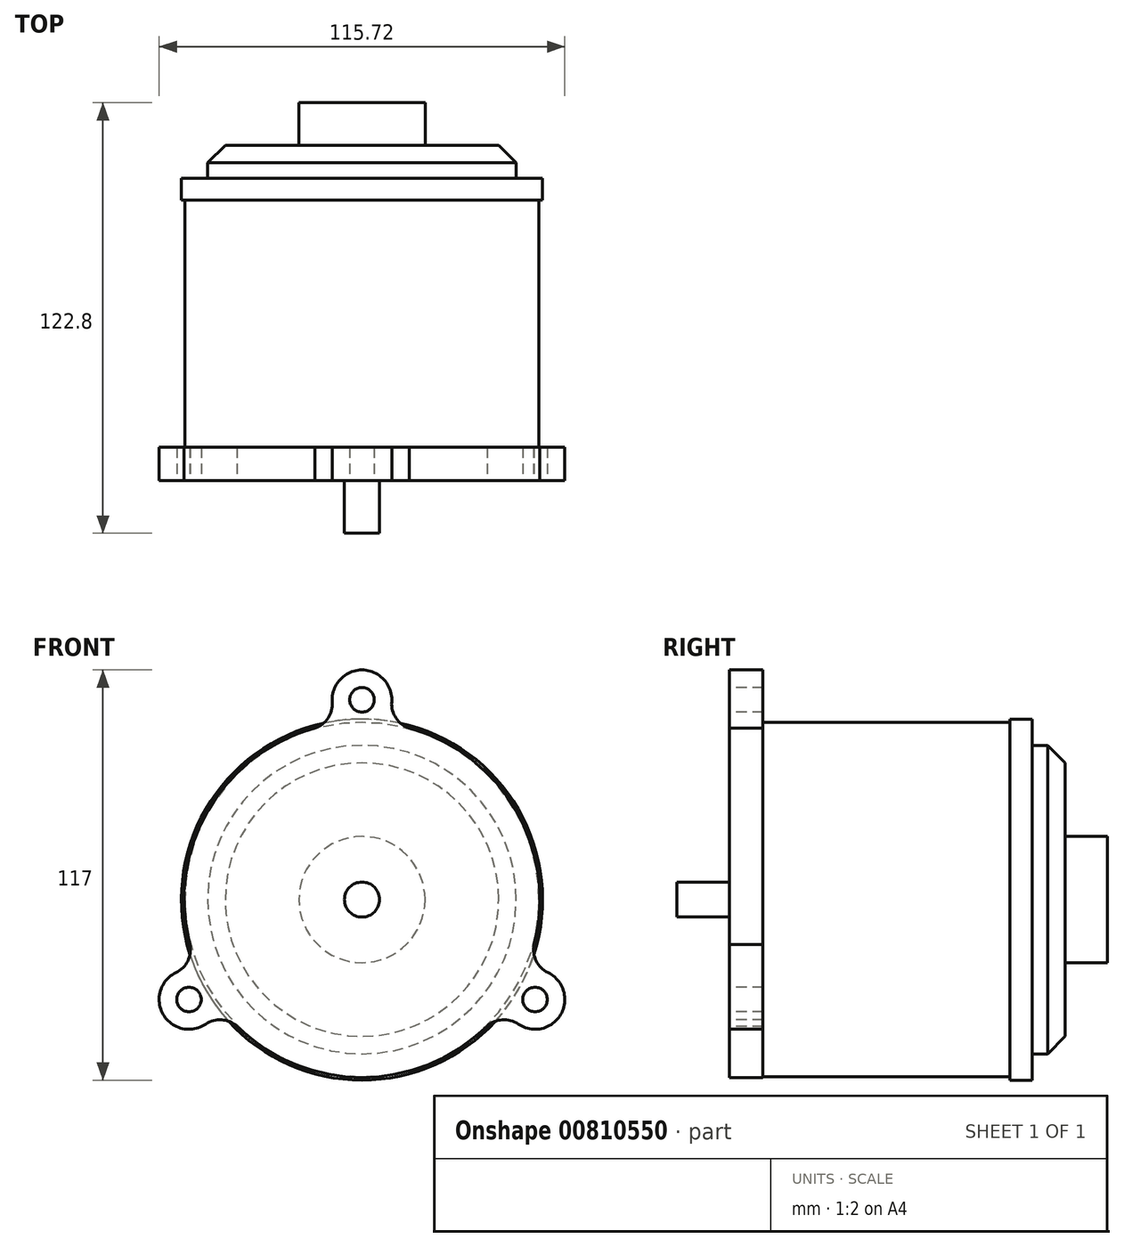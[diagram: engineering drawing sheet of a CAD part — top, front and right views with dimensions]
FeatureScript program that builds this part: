
annotation { "Feature Type Name" : "Feature", "Feature Type Description" : "" }
export const myFeature = defineFeature(function(context is Context, id is Id, definition is map)
    precondition{}
    {
        {
            var Q0;
            Q0=qCreatedBy(makeId("Front.planeOp"),FACE);
            var sketch = newSketch(context, id + "F0", { "sketchPlane" : qUnion([Q0])});
            skCircle(sketch, "E0", {"center": v(0, 0) * mm, "radius": 57 * mm, "construction": true});
            skArc(sketch, "E1", {"start": v(-13.46, 48.93) * mm, "mid": v(-43.95, 25.37) * mm, "end": v(-49.1, -12.81) * mm});
            skLineSegment(sketch, "E2", {"start": v(0, 0) * mm, "end": v(0, 70.33) * mm, "construction": true});
            skCircle(sketch, "E3", {"center": v(0, 57) * mm, "radius": 3.5 * mm});
            skArc(sketch, "E4", {"start": v(8.48, 56.37) * mm, "mid": v(0, 65.5) * mm, "end": v(-8.48, 56.37) * mm});
            skArc(sketch, "E5", {"start": v(-8.48, 56.37) * mm, "mid": v(-9.85, 51.55) * mm, "end": v(-14.03, 48.77) * mm});
            skArc(sketch, "E6", {"start": v(8.48, 56.37) * mm, "mid": v(9.85, 51.55) * mm, "end": v(14.03, 48.77) * mm});
            skArc(sketch, "E7.1.0", {"start": v(-44.58, -35.52) * mm, "mid": v(-39.71, -34.3) * mm, "end": v(-35.22, -36.54) * mm});
            skCircle(sketch, "E7.1.1", {"center": v(-49.36, -28.5) * mm, "radius": 3.5 * mm});
            skArc(sketch, "E7.1.2", {"start": v(-53.05, -20.84) * mm, "mid": v(-56.72, -32.75) * mm, "end": v(-44.58, -35.52) * mm});
            skArc(sketch, "E7.1.3", {"start": v(-53.05, -20.84) * mm, "mid": v(-49.57, -17.24) * mm, "end": v(-49.25, -12.23) * mm});
            skArc(sketch, "E7.2.0", {"start": v(53.05, -20.84) * mm, "mid": v(49.57, -17.24) * mm, "end": v(49.25, -12.23) * mm});
            skCircle(sketch, "E7.2.1", {"center": v(49.36, -28.5) * mm, "radius": 3.5 * mm});
            skArc(sketch, "E7.2.2", {"start": v(44.58, -35.52) * mm, "mid": v(56.72, -32.75) * mm, "end": v(53.05, -20.84) * mm});
            skArc(sketch, "E7.2.3", {"start": v(44.58, -35.52) * mm, "mid": v(39.71, -34.3) * mm, "end": v(35.22, -36.54) * mm});
            skArc(sketch, "E8.trimOffspring", {"start": v(49.1, -12.81) * mm, "mid": v(43.95, 25.37) * mm, "end": v(13.46, 48.93) * mm});
            skArc(sketch, "E9.trimOffspring", {"start": v(-35.65, -36.12) * mm, "mid": v(0, -50.75) * mm, "end": v(35.65, -36.12) * mm});
            skSolve(sketch);
        }
        {
            var Q0;
            Q0=makeQuery(id+"F0.imprint","IMPRINT",FACE,{"disambiguationData":[TD([[makeQuery(id+"F0.imprint","IMPRINT",EDGE,{"derivedFrom":sQuery(id+"F0.wireOp",EDGE,"E3")}),-1.0]])]});
            var sketch = newSketch(context, id + "F1", { "sketchPlane" : qUnion([Q0])});
            skCircle(sketch, "E10", {"center": v(0, 0) * mm, "radius": 5 * mm});
            skSolve(sketch);
        }
        {
            var Q0;
            Q0 = qSketchRegion(id + "F0", true);
            extrude(context, id + "F2", {"entities" : qUnion([Q0]), "oppositeDirection" : true, "depth" : 9.5 * mm, "offsetDistance" : 25 * mm});
        }
        {
            var Q0;
            Q0 = qSketchRegion(id + "F1", true);
            extrude(context, id + "F3", {"entities" : qUnion([Q0]), "operationType" : NewBodyOperationType.ADD, "depth" : 15 * mm, "offsetDistance" : 25 * mm});
        }
        {
            var Q0;
            Q0=makeQuery(id+"F2.opExtrude","CAP_FACE",FACE,{"disambiguationData":[OSD([sQuery(id+"F0.wireOp",EDGE,"E1"),sQuery(id+"F0.wireOp",EDGE,"E3"),sQuery(id+"F0.wireOp",EDGE,"E4"),sQuery(id+"F0.wireOp",EDGE,"E5"),sQuery(id+"F0.wireOp",EDGE,"E6"),sQuery(id+"F0.wireOp",EDGE,"E7.1.0"),sQuery(id+"F0.wireOp",EDGE,"E7.1.1"),sQuery(id+"F0.wireOp",EDGE,"E7.1.2"),sQuery(id+"F0.wireOp",EDGE,"E7.1.3"),sQuery(id+"F0.wireOp",EDGE,"E7.2.0"),sQuery(id+"F0.wireOp",EDGE,"E7.2.1"),sQuery(id+"F0.wireOp",EDGE,"E7.2.2"),sQuery(id+"F0.wireOp",EDGE,"E7.2.3"),sQuery(id+"F0.wireOp",EDGE,"E8.trimOffspring"),sQuery(id+"F0.wireOp",EDGE,"E9.trimOffspring")])],"isStart":false});
            var sketch = newSketch(context, id + "F4", { "sketchPlane" : qUnion([Q0])});
            skCircle(sketch, "E11", {"center": v(0, 0) * mm, "radius": 50.5 * mm});
            skSolve(sketch);
        }
        {
            var Q0;
            Q0 = qSketchRegion(id + "F4", true);
            extrude(context, id + "F5", {"entities" : qUnion([Q0]), "operationType" : NewBodyOperationType.ADD, "depth" : 70.5 * mm, "offsetDistance" : 25 * mm});
        }
        {
            var Q0;
            Q0=makeQuery(id+"F5.opExtrude","CAP_FACE",FACE,{"disambiguationData":[OSD([sQuery(id+"F4.wireOp",EDGE,"E11")])],"isStart":false});
            var sketch = newSketch(context, id + "F6", { "sketchPlane" : qUnion([Q0])});
            skCircle(sketch, "E12", {"center": v(0, 0) * mm, "radius": 51.5 * mm});
            skSolve(sketch);
        }
        {
            var Q0;
            Q0 = qSketchRegion(id + "F6", true);
            extrude(context, id + "F7", {"entities" : qUnion([Q0]), "operationType" : NewBodyOperationType.ADD, "depth" : 6.3 * mm, "offsetDistance" : 25 * mm});
        }
        {
            var Q0;
            Q0=makeQuery(id+"F7.opExtrude","CAP_FACE",FACE,{"disambiguationData":[OSD([sQuery(id+"F6.wireOp",EDGE,"E12")])],"isStart":false});
            var sketch = newSketch(context, id + "F8", { "sketchPlane" : qUnion([Q0])});
            skCircle(sketch, "E13", {"center": v(0, 0) * mm, "radius": 44 * mm});
            skSolve(sketch);
        }
        {
            var Q0;
            Q0 = qSketchRegion(id + "F8", true);
            extrude(context, id + "F9", {"entities" : qUnion([Q0]), "operationType" : NewBodyOperationType.ADD, "depth" : 9.4 * mm, "offsetDistance" : 25 * mm});
        }
        {
            var Q0;
            Q0=makeQuery(id+"F9.opExtrude","CAP_FACE",FACE,{"disambiguationData":[OSD([sQuery(id+"F8.wireOp",EDGE,"E13")])],"isStart":false});
            var sketch = newSketch(context, id + "F10", { "sketchPlane" : qUnion([Q0])});
            skCircle(sketch, "E14", {"center": v(0, 0) * mm, "radius": 18 * mm});
            skSolve(sketch);
        }
        {
            var Q0;
            Q0 = qSketchRegion(id + "F10", true);
            extrude(context, id + "F11", {"entities" : qUnion([Q0]), "operationType" : NewBodyOperationType.ADD, "depth" : 12.1 * mm, "offsetDistance" : 25 * mm});
        }
        {
            var Q0;
            Q0=makeQuery(id+"F3.opExtrude","CAP_FACE",FACE,{"disambiguationData":[OSD([sQuery(id+"F1.wireOp",EDGE,"E10")])],"isStart":false});
            cPlane(context, id + "F12", {"entities" : qUnion([Q0]), "cplaneType" : CPlaneType.OFFSET, "offset" : 1.7 * mm, "oppositeDirection" : true, "width" : 150 * mm, "height" : 150 * mm});
        }
        {
            var Q0;
            Q0=qCreatedBy(id+"F12.planeOp",FACE);
            var sketch = newSketch(context, id + "F13", { "sketchPlane" : qUnion([Q0])});
            skPoint(sketch, "E15", {"position": v(0, 0) * mm});
            skLineSegment(sketch, "E16", {"start": v(0, 0) * mm, "end": v(16.46, -0.71) * mm});
            skSolve(sketch);
        }
        {
            var Q0;
            Q0=sQuery(id+"F13.wireOp",VERTEX,"E15");
            var Q1;
            Q1=sQuery(id+"F13.wireOp",EDGE,"E16");
            cPlane(context, id + "F14", {"entities" : qUnion([Q0, Q1]), "cplaneType" : CPlaneType.LINE_POINT, "offset" : 25 * mm, "width" : 150 * mm, "height" : 150 * mm});
        }
        {
            var Q0;
            Q0=makeQuery(id+"F9.opExtrude","CAP_EDGE",EDGE,{"disambiguationData":[OSD([sQuery(id+"F8.wireOp",EDGE,"E13")])],"isStart":false});
            chamfer(context, id + "F15", {"entities" : qUnion([Q0]), "width" : 5 * mm, "tangentPropagation" : true});
        }
    });
